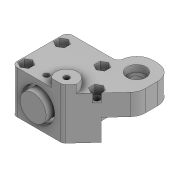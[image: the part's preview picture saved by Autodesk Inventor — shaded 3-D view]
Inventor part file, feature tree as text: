
AUTODESK INVENTOR PART (.ipt)
format: ipt  version: 2022 (Build 260153000, 153)  size: 357,888 bytes
history: native  units: mm
features: extrude x11, sketch x10, projected_geometry x8, fillet x3, plane x1
ambient origin geometry x8: Origin, YZ Plane, XZ Plane, XY Plane, X Axis, Y Axis, Z Axis, Center Point
bodies: Solid1 (feature_tree)
feature tree (33):
  extrude  "Extrusion1"  Depth=12.2mm
  extrude  "Extrusion2"  Depth=2.0mm
  extrude  "Extrusion3"  Depth=2.0mm TaperAngle=0.0deg
  plane  "Work Plane1"
  extrude  "Extrusion4"  Depth=3.0mm
  extrude  "Extrusion6"  Depth=7.0mm
  sketch  "Sketch6"  dims[d12=16.0mm d14=7.0mm]
  extrude  "Extrusion7"  Depth=6.0mm
  extrude  "Extrusion8"  Depth=4.1mm
  fillet  "Fillet1"  Radius=3.0mm
  fillet  "Fillet3"  Radius=4.1mm
  fillet  "Fillet4"  Radius=1.5mm
  extrude  "Extrusion9"  Depth=4.1mm
  extrude  "Extrusion10"  Depth=4.1mm
  extrude  "Extrusion11"  Depth=3.2mm TaperAngle=0.0deg
  extrude  "Extrusion12"  Depth=2.1mm
  sketch  "Sketch1"  dims[d0=9.8mm d1=12.2mm]
  sketch  "Sketch2"  dims[d3=3.0mm d4=2.0mm]
  projected_geometry  "Projected Loop1"
  sketch  "Sketch3"  dims[d5=18.0mm d6=0.0mm d7=2.0mm d8=0.0mm]
  projected_geometry  "Projected Loop2"
  sketch  "Sketch5"  dims[d9=3.0mm d10=0.0mm d11=4.2mm]
  projected_geometry  "Projected Loop3"
  projected_geometry  "Projected Loop4"
  sketch  "Sketch8"  dims[d15=7.0mm d16=6.0mm]
  projected_geometry  "Projected Loop6"
  sketch  "Sketch9"  dims[d17=8.0mm d18=0.0mm d19=4.1mm d21=3.0mm d22=4.1mm d23=1.5mm]
  projected_geometry  "Projected Loop7"
  sketch  "Sketch10"  dims[d26=1.0mm d27=0.0mm d28=4.1mm]
  sketch  "Sketch11"  dims[d29=4.1mm d30=1.5mm]
  projected_geometry  "Projected Loop8"
  sketch  "Sketch12"  dims[d31=1.5mm d32=3.2mm d33=0.0mm d34=2.1mm d35=2.1mm d36=2.1mm d37=2.1mm d38=100.0mm d39=0.0mm d40=6.0mm d42=2.0mm d43=4.0mm d44=1.5mm d45=4.1mm d46=2.1mm d47=8.0mm d48=8.0mm d49=2.1mm d50=3.0mm d51=4.1mm d52=7.1mm d53=2.6mm d54=0.0mm d55=7.1mm d56=2.6mm d57=0.0mm d59=8.2mm d60=0.0mm d62=3.0mm d63=0.0mm d64=3.0mm d65=0.0mm d67=8.0mm]
  projected_geometry  "Projected Loop9"
